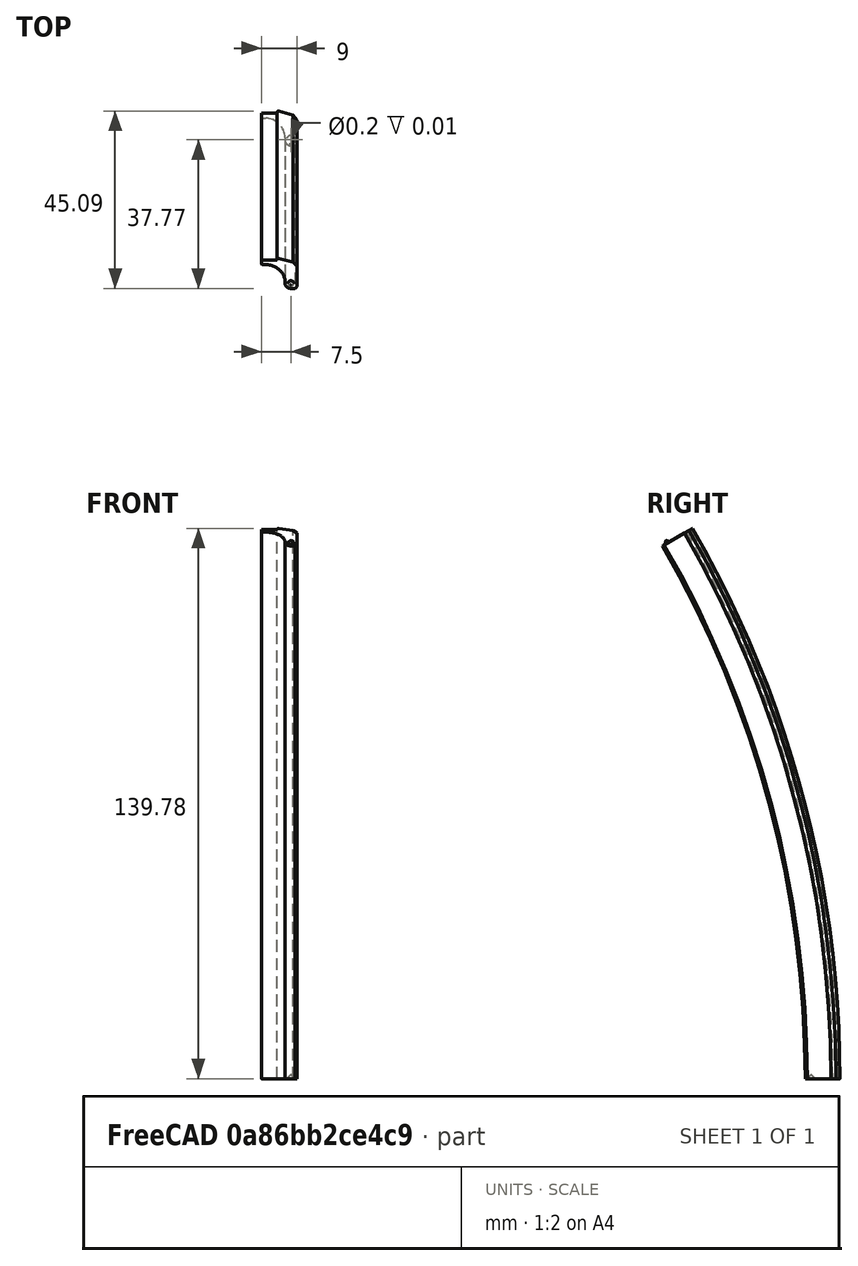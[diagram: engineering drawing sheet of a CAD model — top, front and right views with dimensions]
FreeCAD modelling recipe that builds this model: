
FCSTD DOCUMENT  (FreeCAD 0.16R)
Label: BeadBlock1.2t
License: All rights reserved
LicenseURL: http://en.wikipedia.org/wiki/All_rights_reserved
objects: PartDesign::Fillet×4, PartDesign::Chamfer×4, Sketcher::SketchObject×3, PartDesign::Revolution×1, PartDesign::Pad×1, PartDesign::Pocket×1, Mesh::Feature×1
note: 17 computed .brp shape members not serialized (recipe doc carries the construction recipe); baked Part::Feature solids carry a one-line shape summary decoded from their .brp

FEATURE [Sketcher::SketchObject] Sketch
  sketch-geometry (8):
    g0: LineSegment StartX=0 StartY=279 StartZ=0 EndX=4 EndY=279 EndZ=0
    g1: LineSegment StartX=4 StartY=279 StartZ=0 EndX=4 EndY=279.7 EndZ=0
    g2: LineSegment StartX=0 StartY=277.75 StartZ=0 EndX=0 EndY=279 EndZ=0
    g3: LineSegment StartX=0 StartY=277.75 StartZ=0 EndX=6 EndY=277.75 EndZ=0
    g4: LineSegment StartX=6 StartY=277.75 StartZ=0 EndX=6 EndY=270.75 EndZ=0
    g5: LineSegment StartX=6 StartY=270.75 StartZ=0 EndX=9 EndY=270.75 EndZ=0
    g6: LineSegment StartX=9 StartY=270.75 StartZ=0 EndX=9 EndY=278.25 EndZ=0
    g7: LineSegment StartX=4 StartY=279.7 StartZ=0 EndX=9 EndY=278.25 EndZ=0
  constraints (24):
    c: Horizontal(g0)
    c: PointOnObject(g0,g-2)
    c: DistanceY(g0) = 279
    c: Distance(g0) = 4
    c: Coincident(g1,g0)
    c: Vertical(g1)
    c: Distance(g1) = 0.7
    c: Vertical(g2)
    c: Coincident(g2,g0)
    c: Distance(g2) = 1.25
    c: Horizontal(g3)
    c: Coincident(g3,g2)
    c: Distance(g3) = 6
    c: Vertical(g4)
    c: Coincident(g4,g3)
    c: Distance(g4) = 7
    c: Horizontal(g5)
    c: Coincident(g5,g4)
    c: Distance(g5) = 3
    c: Vertical(g6)
    c: Coincident(g5,g6)
    c: Distance(g6) = 7.5
    c: Coincident(g7,g1)
    c: Coincident(g7,g6)
FEATURE [PartDesign::Revolution] Revolution
  Angle = 30
  Axis = (1,0,0)
  Base = (0,0,0)
  ReferenceAxis = -> Sketch [H_Axis]
  Sketch = -> Sketch
FEATURE [PartDesign::Fillet] Fillet
  Base = -> Revolution [Edge17]
  Radius = 5
FEATURE [PartDesign::Fillet] Fillet001
  Base = -> Fillet [Edge26]
  Radius = 0.4
FEATURE [PartDesign::Fillet] Fillet002
  Base = -> Fillet001 [Edge20]
  Radius = 1.5
FEATURE [PartDesign::Fillet] Fillet003
  Base = -> Fillet002 [Edge27]
  Radius = 0.3
FEATURE [PartDesign::Chamfer] Chamfer
  Base = -> Fillet003 [Edge30]
  Size = 0.5
FEATURE [PartDesign::Chamfer] Chamfer001
  Base = -> Chamfer [Edge21]
  Size = 1
FEATURE [Sketcher::SketchObject] Sketch001
  ExternalGeometry = -> [Chamfer001]
  Placement = pos=(0,0,0) rot=(1,0,0;0.523599rad)
  Support = -> Chamfer001 [Face16]
  sketch-geometry (1):
    g0: Circle CenterX=7.5 CenterY=272.25 CenterZ=0 NormalX=0 NormalY=0 NormalZ=1 Radius=0.75
  constraints (3):
    c: Radius(g0) = 0.75
    c: Distance(g0,g-3) = 1.5
    c: Distance(g0,g-4) = 1.5
FEATURE [PartDesign::Pad] Pad
  Length = 0.75
  Length2 = 100
  Sketch = -> Sketch001
  Type = 0
FEATURE [PartDesign::Chamfer] Chamfer002
  Base = -> Pad [Edge1]
  Size = 0.72
FEATURE [Sketcher::SketchObject] Sketch002
  ExternalGeometry = -> [Chamfer002]
  Placement = pos=(0,0,0) rot=(1,0,0;3.14159rad)
  Support = -> Chamfer002 [Face19]
  sketch-geometry (1):
    g0: Circle CenterX=7.5 CenterY=-272.25 CenterZ=0 NormalX=0 NormalY=0 NormalZ=1 Radius=0.1
  constraints (3):
    c: Distance(g0,g-4) = 1.5
    c: Distance(g0,g-3) = 1.5
    c: Radius(g0) = 0.1
FEATURE [PartDesign::Pocket] Pocket
  Length = 1
  Sketch = -> Sketch002
  Type = 0
FEATURE [PartDesign::Chamfer] Chamfer003
  Base = -> Pocket [Edge48]
  Size = 0.99
FEATURE [Mesh::Feature] Mesh  label="Chamfer003 (Meshed)"
